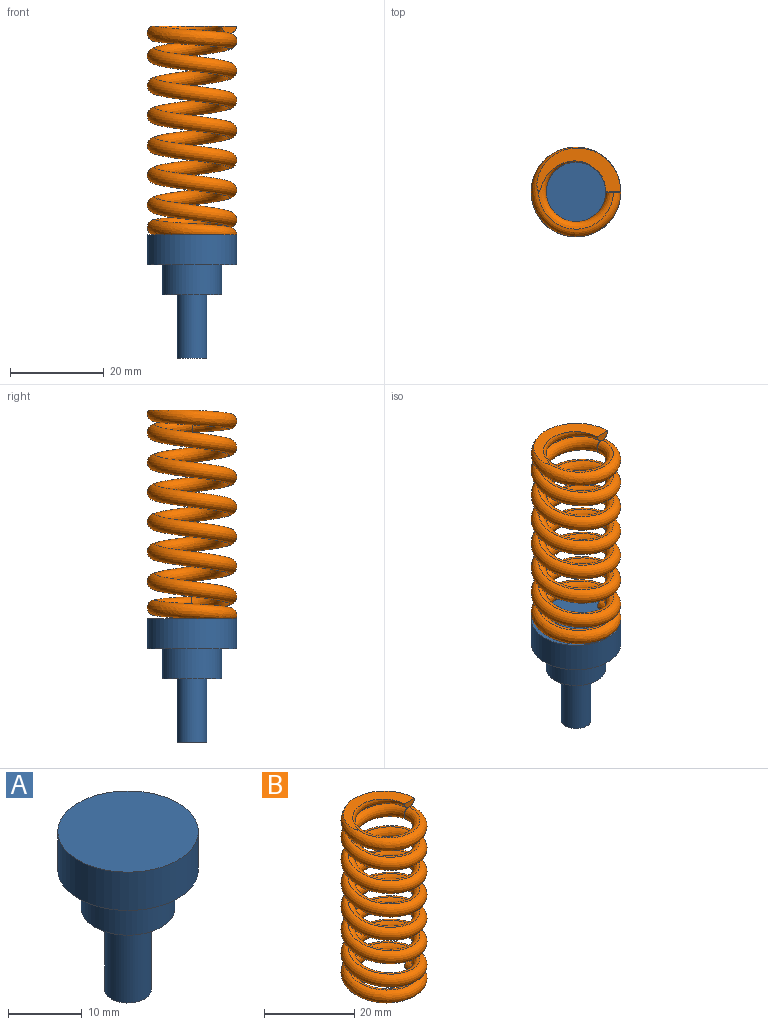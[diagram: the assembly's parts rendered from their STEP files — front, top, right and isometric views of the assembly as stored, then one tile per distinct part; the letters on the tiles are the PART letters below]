
ASSEMBLY  parts=2 mates=1
PART A: 7 faces, bbox 19.1x19.1x26.2 mm
  f0: cylinder r=9.53mm len=19.05mm, axis (0,0,1), area 380mm2, adj f1,f2
  f1: plane 19.05x19.05mm, normal (0,0,-1), area 158.3mm2, adj f0,f3
  f2: plane 19.05x19.05mm, normal (0,0,1), area 285mm2, adj f0
  f3: cylinder r=6.35mm len=12.7mm, axis (0,0,1), area 253.4mm2, adj f1,f4
  f4: plane 12.7x12.7mm, normal (0,0,-1), area 95mm2, adj f3,f5
  f5: cylinder r=3.17mm len=13.49mm, axis (0,0,1), area 269.2mm2, adj f4,f6
  f6: plane 6.35x6.35mm, normal (0,0,-1), area 31.7mm2, adj f5
PART B: 10 faces, bbox 24.2x24.3x49.4 mm
  f0: bspline ~22.48x22.35mm, area 251.5mm2, adj f1,f6,f7,f8
  f1: bspline ~41.23x22.37mm, area 1695.6mm2, adj f0,f2,f5
  f2: bspline ~18.91x18.9mm, area 251mm2, adj f1,f3,f4,f9
  f3: bspline ~16.06x15.97mm, area 192.5mm2, adj f2,f4,f5,f9
  f4: plane 3.63x2.04mm, normal (0,-1,0), area 4mm2, adj f2,f3,f9
  f5: bspline ~41.22x15.98mm, area 1317mm2, adj f1,f3,f7
  f6: plane 3.18x1.59mm, normal (0,1,-0.05), area 4mm2, adj f0,f7,f8
  f7: bspline ~15.87x15.87mm, area 193mm2, adj f0,f5,f6,f8
  f8: plane 19.63x11.1mm, normal (0,0,-1), area 61.9mm2, adj f0,f6,f7
  f9: plane 19.62x11.11mm, normal (0,0,1), area 61.6mm2, adj f2,f3,f4
PLACE A at identity fixed
PLACE B rot(axis=(1,0,0),180deg) t=(0,0,25.4)mm
MATE fastened B.f9 <-> A.f0  axis (0,0,-1) through (0,0,25.4)mm
